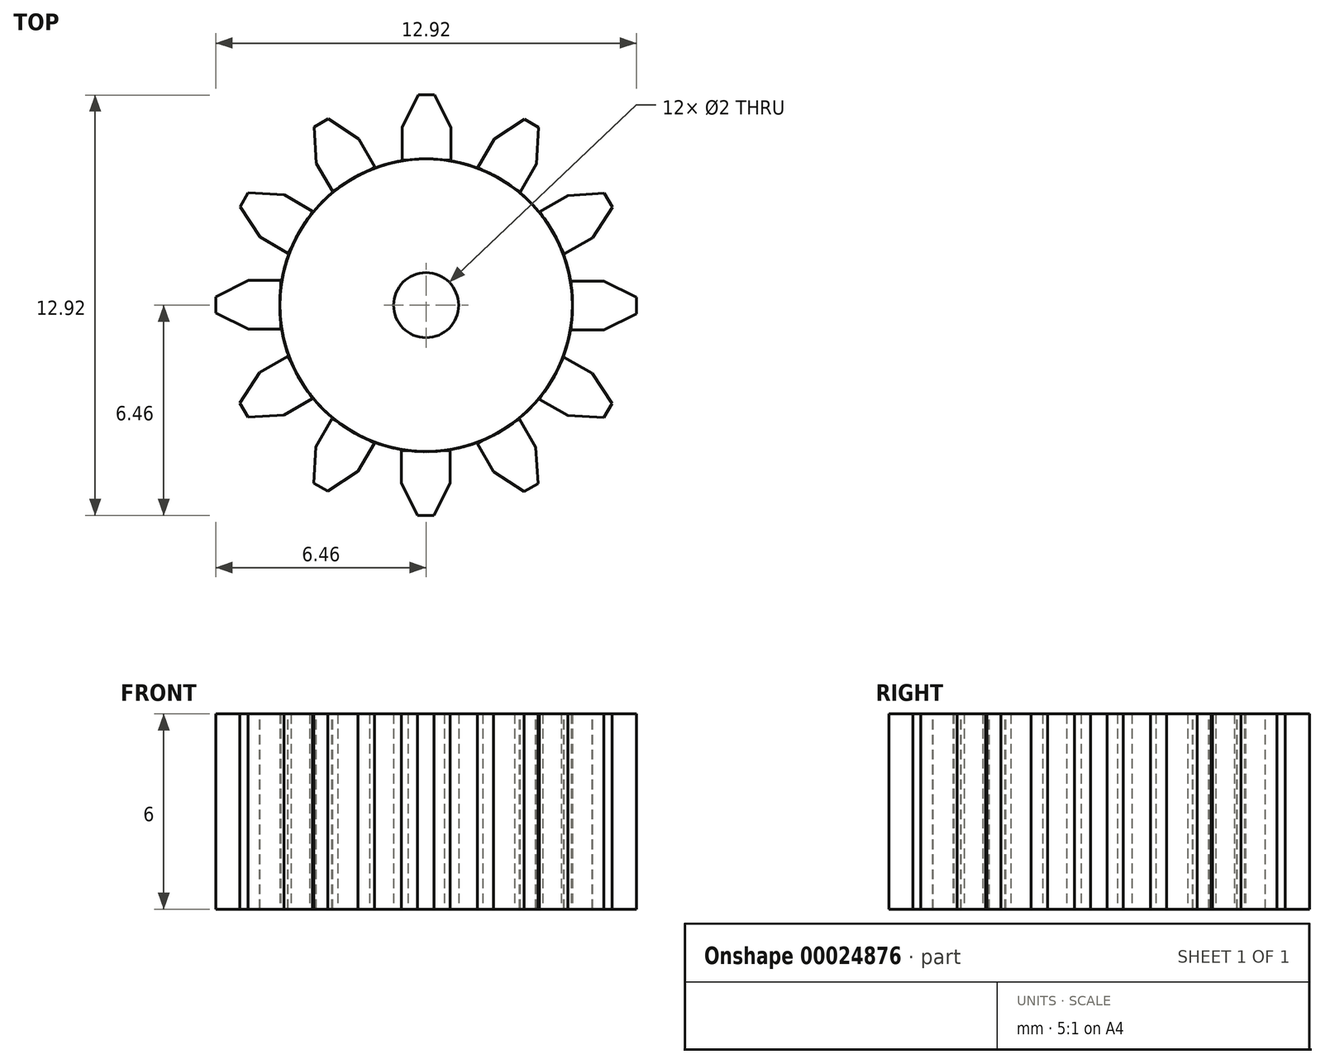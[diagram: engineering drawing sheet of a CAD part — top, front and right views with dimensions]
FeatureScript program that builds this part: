
annotation { "Feature Type Name" : "Feature", "Feature Type Description" : "" }
export const myFeature = defineFeature(function(context is Context, id is Id, definition is map)
    precondition{}
    {
        {
            var Q0;
            Q0=qCreatedBy(makeId("Top.planeOp"),FACE);
            var sketch = newSketch(context, id + "F0", { "sketchPlane" : qUnion([Q0])});
            skCircle(sketch, "E0", {"center": v(0, 0) * mm, "radius": 1 * mm});
            skCircle(sketch, "E1", {"center": v(0, 0) * mm, "radius": 4.5 * mm});
            skLineSegment(sketch, "E2.bottom", {"start": v(0.87, 4.42) * mm, "end": v(-0.63, 4.42) * mm});
            skSolve(sketch);
        }
        {
            var Q0;
            Q0 = qSketchRegion(id + "F0", true);
            extrude(context, id + "F1", {"entities" : qUnion([Q0]), "depth" : 6 * mm});
        }
        {
            var Q0;
            Q0=makeQuery(id+"F1.opExtrude","CAP_FACE",FACE,{"disambiguationData":[OSD([sQuery(id+"F0.wireOp",EDGE,"E0"),sQuery(id+"F0.wireOp",EDGE,"E1")])],"isStart":false});
            var sketch = newSketch(context, id + "F2", { "sketchPlane" : qUnion([Q0])});
            skLineSegment(sketch, "E3", {"start": v(0.26, 6.46) * mm, "end": v(0.76, 5.46) * mm});
            skLineSegment(sketch, "E4.bottom", {"start": v(0.76, 4.46) * mm, "end": v(-0.74, 4.46) * mm});
            skLineSegment(sketch, "E4.left", {"start": v(0.76, 4.46) * mm, "end": v(0.76, 6.46) * mm});
            skLineSegment(sketch, "E5", {"start": v(-0.74, 5.46) * mm, "end": v(-0.24, 6.46) * mm});
            skLineSegment(sketch, "E4.right", {"start": v(-0.74, 4.46) * mm, "end": v(-0.74, 6.46) * mm});
            skLineSegment(sketch, "E4.top", {"start": v(0.76, 6.46) * mm, "end": v(-0.74, 6.46) * mm});
            skSolve(sketch);
        }
        {
            var Q0;
            {var subQ0=makeQuery(id+"F1.opExtrude","CAP_EDGE",EDGE,{"disambiguationData":[OSD([sQuery(id+"F0.wireOp",EDGE,"E1")])],"isStart":false});var subQ1=sQuery(id+"F2.wireOp",EDGE,"E4.bottom");var subQ3=makeQuery(id+"F2.imprint","INTERSECT",VERTEX,{"disambiguationData":[OD(0.0)],"derivedFrom":[subQ0,subQ1]});Q0=makeQuery(id+"F2.imprint","IMPRINT",FACE,{"disambiguationData":[TD([[makeQuery(id+"F2.imprint","IMPRINT",EDGE,{"disambiguationData":[TD([[subQ3,-1.0]])],"derivedFrom":subQ1}),-1.0]])]});}
            var Q1;
            {var subQ6=sQuery(id+"F2.wireOp",EDGE,"E3");Q1=makeQuery(id+"F2.imprint","IMPRINT",FACE,{"disambiguationData":[TD([[makeQuery(id+"F2.imprint","IMPRINT",EDGE,{"derivedFrom":subQ6}),-1.0]])]});}
            extrude(context, id + "F3", {"entities" : qUnion([Q0, Q1]), "operationType" : NewBodyOperationType.ADD, "oppositeDirection" : true, "depth" : 6 * mm});
        }
        {
            var Q0;
            Q0=makeQuery(id+"F1.opExtrude","SWEPT_BODY",BODY,{"disambiguationData":[OSD([sQuery(id+"F0.wireOp",EDGE,"E0"),sQuery(id+"F0.wireOp",EDGE,"E1")])]});
            var Q1;
            Q1=makeQuery(id+"F1.opExtrude","CAP_EDGE",EDGE,{"disambiguationData":[OSD([sQuery(id+"F0.wireOp",EDGE,"E0")])],"isStart":false});
            circularPattern(context, id + "F4", {"entities" : qUnion([Q0]), "axis" : qUnion([Q1]), "angle" : 30 * degree, "instanceCount" : 12});
        }
    });
